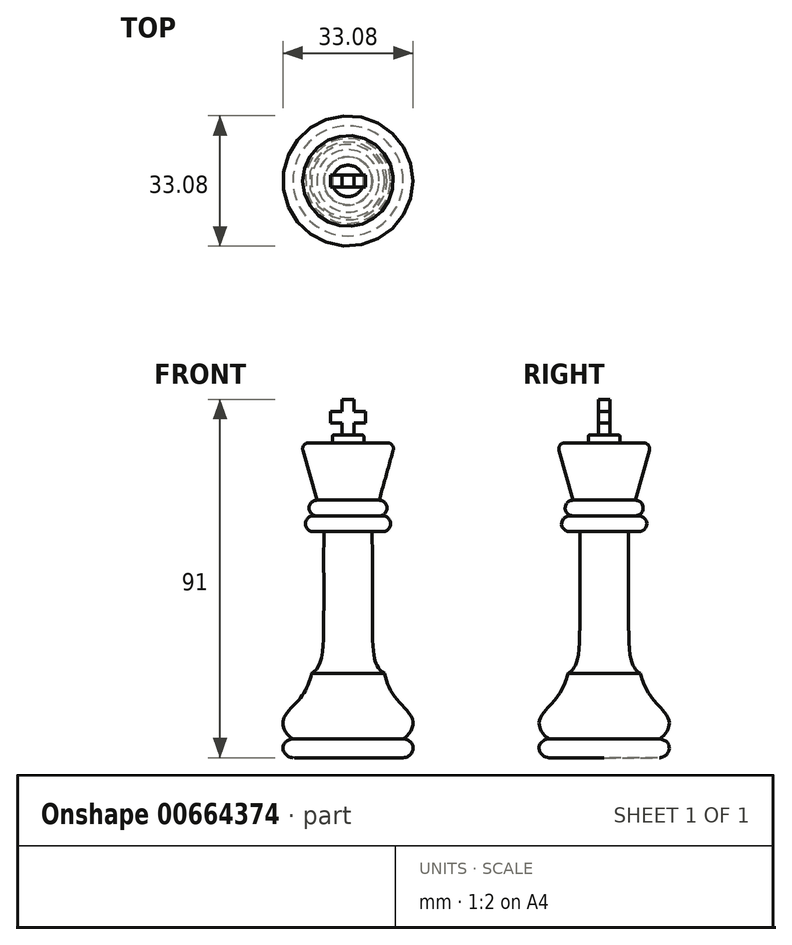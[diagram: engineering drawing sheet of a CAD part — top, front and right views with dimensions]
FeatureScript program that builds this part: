
annotation { "Feature Type Name" : "Feature", "Feature Type Description" : "" }
export const myFeature = defineFeature(function(context is Context, id is Id, definition is map)
    precondition{}
    {
        {
            var Q0;
            Q0=qCreatedBy(makeId("Front.planeOp"),FACE);
            var sketch = newSketch(context, id + "F0", { "sketchPlane" : qUnion([Q0])});
            skLineSegment(sketch, "E0", {"start": v(0, 0) * mm, "end": v(14, 0) * mm});
            skFitSpline(sketch, "E1", {"points": [v(14, 0) * mm, v(16.54, 2.54) * mm, v(14, 4.8) * mm], "startDerivative": vector(8.82, 0) * mm, "endDerivative": vector(-8.91, 0.72) * mm});
            skFitSpline(sketch, "E2", {"points": [v(14, 4.8) * mm, v(16.54, 8.78) * mm, v(12.69, 14.5) * mm, v(9.26, 21.41) * mm], "startDerivative": vector(11.17, 4.25) * mm, "endDerivative": vector(-4, 21.15) * mm});
            skFitSpline(sketch, "E3", {"points": [v(9.26, 21.41) * mm, v(7.3, 23.57) * mm, v(6.41, 27.39) * mm, v(6.13, 57.43) * mm], "startDerivative": vector(-15.43, 6.56) * mm, "endDerivative": vector(-0.61, 47.18) * mm});
            skLineSegment(sketch, "E4", {"start": v(6.13, 57.43) * mm, "end": v(8.82, 57.43) * mm});
            skArc(sketch, "E5", {"start": v(8.82, 57.43) * mm, "mid": v(10.82, 59.43) * mm, "end": v(8.82, 61.43) * mm});
            skLineSegment(sketch, "E6", {"start": v(8.82, 61.43) * mm, "end": v(7.92, 61.43) * mm});
            skArc(sketch, "E7", {"start": v(7.92, 61.43) * mm, "mid": v(9.9, 63.43) * mm, "end": v(7.92, 65.42) * mm});
            skLineSegment(sketch, "E8", {"start": v(7.92, 65.42) * mm, "end": v(12, 80) * mm});
            skLineSegment(sketch, "E9", {"start": v(12, 80) * mm, "end": v(0, 80) * mm});
            skLineSegment(sketch, "E10", {"start": v(0, 80) * mm, "end": v(0, 0) * mm});
            skSolve(sketch);
        }
        {
            var Q0;
            Q0 = qSketchRegion(id + "F0", true);
            var Q1;
            Q1=sQuery(id+"F0.wireOp",EDGE,"E10");
            revolve(context, id + "F1", {"surfaceOperationType" : NewSurfaceOperationType.NEW, "entities" : qUnion([Q0]), "axis" : qUnion([Q1]), "revolveType" : RevolveType.FULL});
        }
        {
            var Q0;
            Q0=makeQuery(id+"F1.opRevolve","SWEPT_EDGE",EDGE,{"disambiguationData":[OSD([sQuery(id+"F0.wireOp",EDGE,"E8"),sQuery(id+"F0.wireOp",EDGE,"E9")])]});
            fillet(context, id + "F2", {"entities" : qUnion([Q0]), "radius" : 1.5 * mm, "tangentPropagation" : true, "allowEdgeOverflow" : false});
        }
        {
            var Q0;
            Q0=qCreatedBy(makeId("Top.planeOp"),FACE);
            cPlane(context, id + "F3", {"entities" : qUnion([Q0]), "cplaneType" : CPlaneType.OFFSET, "offset" : 80 * mm, "width" : 150 * mm, "height" : 150 * mm});
        }
        {
            var Q0;
            Q0=qCreatedBy(id+"F3.planeOp",FACE);
            var sketch = newSketch(context, id + "F4", { "sketchPlane" : qUnion([Q0])});
            skCircle(sketch, "E11", {"center": v(0, 0) * mm, "radius": 4 * mm});
            skSolve(sketch);
        }
        {
            var Q0;
            Q0 = qSketchRegion(id + "F4", true);
            extrude(context, id + "F5", {"entities" : qUnion([Q0]), "operationType" : NewBodyOperationType.ADD, "depth" : 2 * mm, "offsetDistance" : 25 * mm});
        }
        {
            var Q0;
            Q0=qCreatedBy(makeId("Top.planeOp"),FACE);
            cPlane(context, id + "F6", {"entities" : qUnion([Q0]), "cplaneType" : CPlaneType.OFFSET, "offset" : 82 * mm, "width" : 150 * mm, "height" : 150 * mm});
        }
        {
            var Q0;
            Q0=qCreatedBy(id+"F6.planeOp",FACE);
            var sketch = newSketch(context, id + "F7", { "sketchPlane" : qUnion([Q0])});
            skLineSegment(sketch, "E12", {"start": v(0, 0) * mm, "end": v(0, -1.5) * mm, "construction": true});
            skLineSegment(sketch, "E13", {"start": v(0, -1.5) * mm, "end": v(-1.5, -1.5) * mm});
            skLineSegment(sketch, "E14", {"start": v(-1.5, -1.5) * mm, "end": v(1.5, -1.5) * mm});
            skSolve(sketch);
        }
        {
            var Q0;
            Q0=qCreatedBy(makeId("Front.planeOp"),FACE);
            cPlane(context, id + "F8", {"entities" : qUnion([Q0]), "cplaneType" : CPlaneType.OFFSET, "offset" : 1.5 * mm, "width" : 150 * mm, "height" : 150 * mm});
        }
        {
            var Q0;
            Q0=qCreatedBy(id+"F8.planeOp",FACE);
            var sketch = newSketch(context, id + "F9", { "sketchPlane" : qUnion([Q0])});
            skLineSegment(sketch, "E15", {"start": v(-1.5, 82) * mm, "end": v(-1.5, 85) * mm});
            skLineSegment(sketch, "E16", {"start": v(-1.5, 85) * mm, "end": v(-4.5, 85) * mm});
            skLineSegment(sketch, "E17", {"start": v(-4.5, 85) * mm, "end": v(-4.5, 88) * mm});
            skLineSegment(sketch, "E18", {"start": v(-4.5, 88) * mm, "end": v(-1.5, 88) * mm});
            skLineSegment(sketch, "E19", {"start": v(-1.5, 88) * mm, "end": v(-1.5, 91) * mm});
            skLineSegment(sketch, "E20.MirrorCS", {"start": v(1.5, 82) * mm, "end": v(1.5, 85) * mm});
            skLineSegment(sketch, "E21.MirrorCS", {"start": v(1.5, 85) * mm, "end": v(4.5, 85) * mm});
            skLineSegment(sketch, "E22.MirrorCS", {"start": v(4.5, 85) * mm, "end": v(4.5, 88) * mm});
            skLineSegment(sketch, "E23.MirrorCS", {"start": v(4.5, 88) * mm, "end": v(1.5, 88) * mm});
            skLineSegment(sketch, "E24.MirrorCS", {"start": v(1.5, 88) * mm, "end": v(1.5, 91) * mm});
            skLineSegment(sketch, "E25", {"start": v(-1.5, 91) * mm, "end": v(1.5, 91) * mm});
            skLineSegment(sketch, "E26", {"start": v(-1.5, 82) * mm, "end": v(1.5, 82) * mm});
            skSolve(sketch);
        }
        {
            var Q0;
            Q0 = qSketchRegion(id + "F9", true);
            extrude(context, id + "F10", {"entities" : qUnion([Q0]), "operationType" : NewBodyOperationType.ADD, "oppositeDirection" : true, "depth" : 3 * mm, "offsetDistance" : 25 * mm});
        }
        {
            var Q0;
            Q0=makeQuery(id+"F5.opExtrude","CAP_EDGE",EDGE,{"disambiguationData":[OSD([sQuery(id+"F4.wireOp",EDGE,"E11")])],"isStart":false});
            fillet(context, id + "F11", {"entities" : qUnion([Q0]), "radius" : .4 * mm, "tangentPropagation" : true, "allowEdgeOverflow" : false});
        }
    });
